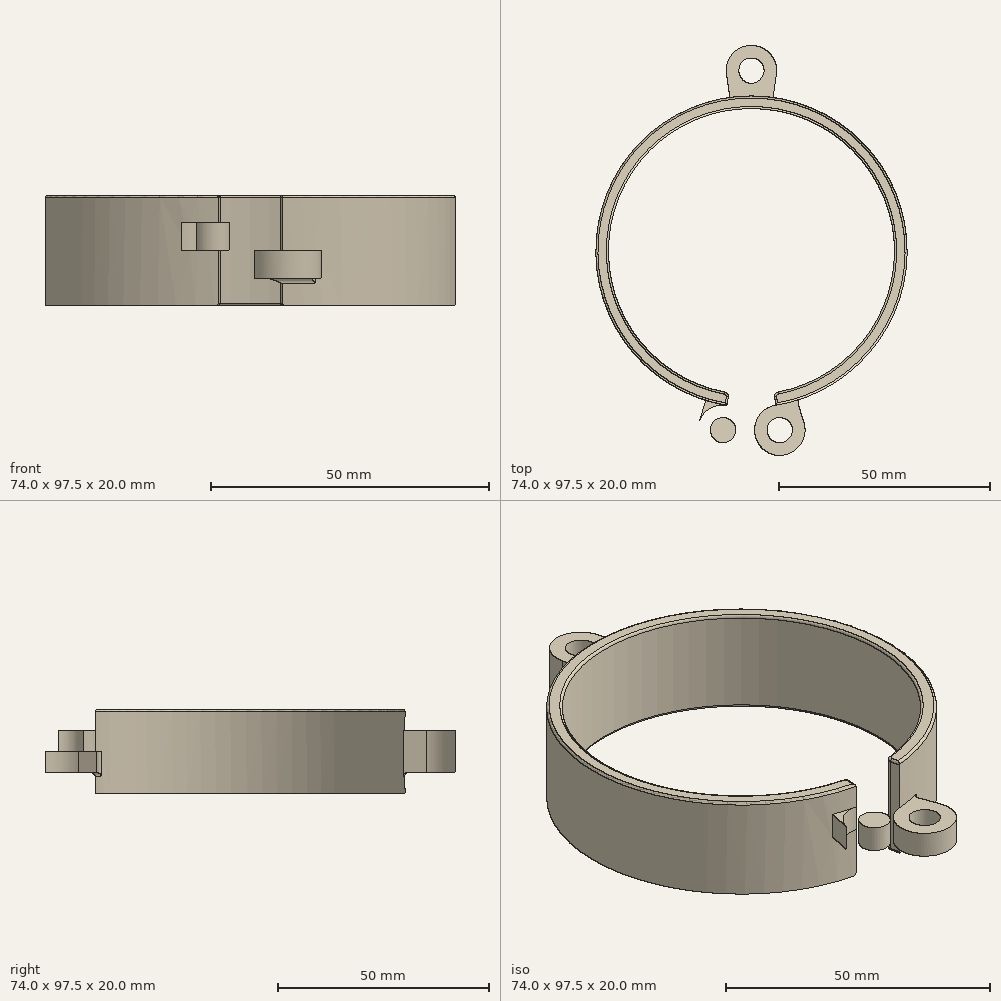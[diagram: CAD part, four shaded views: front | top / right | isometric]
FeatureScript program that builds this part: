
annotation { "Feature Type Name" : "Feature", "Feature Type Description" : "" }
export const myFeature = defineFeature(function(context is Context, id is Id, definition is map)
    precondition{}
    {
        {
            var Q0;
            Q0=qCreatedBy(makeId("Right.planeOp"),FACE);
            var sketch = newSketch(context, id + "F0", { "sketchPlane" : qUnion([Q0])});
            skLineSegment(sketch, "E0.bottom", {"start": v(34, 0) * mm, "end": v(37, 0) * mm});
            skLineSegment(sketch, "E0.top", {"start": v(34, 20) * mm, "end": v(37, 20) * mm});
            skLineSegment(sketch, "E0.left", {"start": v(34, 0) * mm, "end": v(34, 20) * mm});
            skLineSegment(sketch, "E0.right", {"start": v(37, 0) * mm, "end": v(37, 20) * mm});
            skLineSegment(sketch, "E1", {"start": v(0, 0) * mm, "end": v(0, 41.8) * mm, "construction": true});
            skSolve(sketch);
        }
        {
            var Q0;
            Q0=makeQuery(id+"F0.imprint","IMPRINT",FACE,{"disambiguationData":[TD([[makeQuery(id+"F0.imprint","IMPRINT",EDGE,{"derivedFrom":sQuery(id+"F0.wireOp",EDGE,"E0.bottom")}),1.0]])]});
            var Q1;
            Q1=sQuery(id+"F0.wireOp",EDGE,"E1");
            revolve(context, id + "F1", {"entities" : qUnion([Q0]), "axis" : qUnion([Q1]), "revolveType" : RevolveType.SYMMETRIC, "angle" : 342 * degree});
        }
        {
            var Q0;
            Q0=qCreatedBy(makeId("Top.planeOp"),FACE);
            var sketch = newSketch(context, id + "F2", { "sketchPlane" : qUnion([Q0])});
            skArc(sketch, "E2.0", {"start": v(-5.79, -36.54) * mm, "mid": v(0, 37) * mm, "end": v(5.79, -36.54) * mm});
            skLineSegment(sketch, "E3", {"start": v(0, 0) * mm, "end": v(0, -68.45) * mm, "construction": true});
            skLineSegment(sketch, "E4", {"start": v(0, 0) * mm, "end": v(0.74, -42.57) * mm, "construction": true});
            skLineSegment(sketch, "E5", {"start": v(10.84, -35.37) * mm, "end": v(12.48, -40.71) * mm});
            skCircle(sketch, "E6", {"center": v(6.74, -42.47) * mm, "radius": 6 * mm});
            skPoint(sketch, "E6.first.point", {"position": v(0.74, -42.57) * mm});
            skPoint(sketch, "E6.second.point", {"position": v(12.48, -40.71) * mm});
            skPoint(sketch, "E6.third.point", {"position": v(5.8, -36.54) * mm});
            skCircle(sketch, "E7.0", {"center": v(6.74, -42.47) * mm, "radius": 3 * mm});
            skLineSegment(sketch, "E8", {"start": v(5.79, -36.54) * mm, "end": v(5.79, -36.54) * mm});
            skCircle(sketch, "E9.MirrorC", {"center": v(-6.74, -42.47) * mm, "radius": 6 * mm});
            skCircle(sketch, "E10.MirrorC", {"center": v(-6.74, -42.47) * mm, "radius": 3 * mm});
            skLineSegment(sketch, "E11.MirrorCS", {"start": v(-10.84, -35.37) * mm, "end": v(-12.48, -40.71) * mm});
            skLineSegment(sketch, "E12.MirrorCS", {"start": v(-5.79, -36.54) * mm, "end": v(-5.79, -36.54) * mm});
            skPoint(sketch, "E13.orphan", {"position": v(20.87, -68.1) * mm});
            skPoint(sketch, "E14.orphan", {"position": v(-20.87, -68.1) * mm});
            skLineSegment(sketch, "E15", {"start": v(0, 0) * mm, "end": v(0, 59.86) * mm, "construction": true});
            skLineSegment(sketch, "E16", {"start": v(5.16, 36.64) * mm, "end": v(5.94, 42.16) * mm});
            skLineSegment(sketch, "E17.MirrorCS", {"start": v(-5.16, 36.64) * mm, "end": v(-5.94, 42.16) * mm});
            skCircle(sketch, "E18", {"center": v(0, 43) * mm, "radius": 6 * mm});
            skPoint(sketch, "E18.first.point", {"position": v(-5.94, 42.16) * mm});
            skPoint(sketch, "E18.second.point", {"position": v(5.94, 42.16) * mm});
            skPoint(sketch, "E18.third.point", {"position": v(0, 37) * mm});
            skCircle(sketch, "E19.0", {"center": v(0, 43) * mm, "radius": 3 * mm});
            skPoint(sketch, "E20.orphan", {"position": v(-8.52, 60.47) * mm});
            skPoint(sketch, "E21.orphan", {"position": v(8.52, 60.47) * mm});
            skLineSegment(sketch, "E22", {"start": v(0, 0) * mm, "end": v(6.74, -42.47) * mm, "construction": true});
            skSolve(sketch);
        }
        {
            var Q0;
            Q0=makeQuery(id+"F2.imprint","IMPRINT",FACE,{"disambiguationData":[TD([[makeQuery(id+"F2.imprint","IMPRINT",EDGE,{"derivedFrom":sQuery(id+"F2.wireOp",EDGE,"E7.0")}),-1.0]])]});
            var Q1;
            {var subQ0=sQuery(id+"F2.wireOp",EDGE,"E8");Q1=makeQuery(id+"F2.imprint","IMPRINT",FACE,{"disambiguationData":[TD([[makeQuery(id+"F2.imprint","IMPRINT",EDGE,{"derivedFrom":subQ0}),1.0]])]});}
            var Q2;
            {var subQ0=sQuery(id+"F2.wireOp",EDGE,"E5");Q2=makeQuery(id+"F2.imprint","IMPRINT",FACE,{"disambiguationData":[TD([[makeQuery(id+"F2.imprint","IMPRINT",EDGE,{"derivedFrom":subQ0}),-1.0]])]});}
            extrude(context, id + "F3", {"entities" : qUnion([Q0, Q1, Q2]), "operationType" : NewBodyOperationType.ADD, "depth" : 10 * mm});
        }
        {
            var Q0;
            {var subQ0=sQuery(id+"F2.wireOp",EDGE,"E12.MirrorCS");Q0=makeQuery(id+"F2.imprint","IMPRINT",FACE,{"disambiguationData":[TD([[makeQuery(id+"F2.imprint","IMPRINT",EDGE,{"derivedFrom":subQ0}),-1.0]])]});}
            var Q1;
            {var subQ0=sQuery(id+"F2.wireOp",EDGE,"E11.MirrorCS");Q1=makeQuery(id+"F2.imprint","IMPRINT",FACE,{"disambiguationData":[TD([[makeQuery(id+"F2.imprint","IMPRINT",EDGE,{"derivedFrom":subQ0}),1.0]])]});}
            var Q2;
            Q2=makeQuery(id+"F2.imprint","IMPRINT",FACE,{"disambiguationData":[TD([[makeQuery(id+"F2.imprint","IMPRINT",EDGE,{"derivedFrom":sQuery(id+"F2.wireOp",EDGE,"E10.MirrorC")}),1.0]])]});
            extrude(context, id + "F4", {"entities" : qUnion([Q0, Q1, Q2]), "operationType" : NewBodyOperationType.ADD, "depth" : 15 * mm});
        }
        {
            var Q0;
            {var subQ0=sQuery(id+"F2.wireOp",EDGE,"E12.MirrorCS");Q0=makeQuery(id+"F2.imprint","IMPRINT",FACE,{"disambiguationData":[TD([[makeQuery(id+"F2.imprint","IMPRINT",EDGE,{"derivedFrom":subQ0}),-1.0]])]});}
            var Q1;
            {var subQ0=sQuery(id+"F2.wireOp",EDGE,"E11.MirrorCS");Q1=makeQuery(id+"F2.imprint","IMPRINT",FACE,{"disambiguationData":[TD([[makeQuery(id+"F2.imprint","IMPRINT",EDGE,{"derivedFrom":subQ0}),1.0]])]});}
            var Q2;
            Q2=makeQuery(id+"F2.imprint","IMPRINT",FACE,{"disambiguationData":[TD([[makeQuery(id+"F2.imprint","IMPRINT",EDGE,{"derivedFrom":sQuery(id+"F2.wireOp",EDGE,"E10.MirrorC")}),1.0]])]});
            extrude(context, id + "F5", {"entities" : qUnion([Q0, Q1, Q2]), "operationType" : NewBodyOperationType.REMOVE, "depth" : 10 * mm});
        }
        {
            var Q0;
            {var subQ0=sQuery(id+"F2.wireOp",EDGE,"E8");Q0=makeQuery(id+"F2.imprint","IMPRINT",FACE,{"disambiguationData":[TD([[makeQuery(id+"F2.imprint","IMPRINT",EDGE,{"derivedFrom":subQ0}),1.0]])]});}
            var Q1;
            Q1=makeQuery(id+"F2.imprint","IMPRINT",FACE,{"disambiguationData":[TD([[makeQuery(id+"F2.imprint","IMPRINT",EDGE,{"derivedFrom":sQuery(id+"F2.wireOp",EDGE,"E7.0")}),-1.0]])]});
            var Q2;
            {var subQ0=sQuery(id+"F2.wireOp",EDGE,"E5");Q2=makeQuery(id+"F2.imprint","IMPRINT",FACE,{"disambiguationData":[TD([[makeQuery(id+"F2.imprint","IMPRINT",EDGE,{"derivedFrom":subQ0}),-1.0]])]});}
            extrude(context, id + "F6", {"entities" : qUnion([Q0, Q1, Q2]), "operationType" : NewBodyOperationType.REMOVE, "depth" : 5 * mm});
        }
        {
            var Q0;
            Q0=makeQuery(id+"F2.imprint","IMPRINT",FACE,{"disambiguationData":[TD([[makeQuery(id+"F2.imprint","IMPRINT",EDGE,{"derivedFrom":sQuery(id+"F2.wireOp",EDGE,"E19.0")}),-1.0]])]});
            var Q1;
            {var subQ0=sQuery(id+"F2.wireOp",EDGE,"E17.MirrorCS");Q1=makeQuery(id+"F2.imprint","IMPRINT",FACE,{"disambiguationData":[TD([[makeQuery(id+"F2.imprint","IMPRINT",EDGE,{"derivedFrom":subQ0}),-1.0]])]});}
            var Q2;
            {var subQ0=sQuery(id+"F2.wireOp",EDGE,"E16");Q2=makeQuery(id+"F2.imprint","IMPRINT",FACE,{"disambiguationData":[TD([[makeQuery(id+"F2.imprint","IMPRINT",EDGE,{"derivedFrom":subQ0}),1.0]])]});}
            extrude(context, id + "F7", {"entities" : qUnion([Q0, Q1, Q2]), "operationType" : NewBodyOperationType.ADD, "depth" : 15 * mm});
        }
        {
            var Q0;
            Q0=makeQuery(id+"F2.imprint","IMPRINT",FACE,{"disambiguationData":[TD([[makeQuery(id+"F2.imprint","IMPRINT",EDGE,{"derivedFrom":sQuery(id+"F2.wireOp",EDGE,"E19.0")}),1.0]])]});
            var Q1;
            Q1=makeQuery(id+"F2.imprint","IMPRINT",FACE,{"disambiguationData":[TD([[makeQuery(id+"F2.imprint","IMPRINT",EDGE,{"derivedFrom":sQuery(id+"F2.wireOp",EDGE,"E19.0")}),-1.0]])]});
            var Q2;
            {var subQ0=sQuery(id+"F2.wireOp",EDGE,"E17.MirrorCS");Q2=makeQuery(id+"F2.imprint","IMPRINT",FACE,{"disambiguationData":[TD([[makeQuery(id+"F2.imprint","IMPRINT",EDGE,{"derivedFrom":subQ0}),-1.0]])]});}
            var Q3;
            {var subQ0=sQuery(id+"F2.wireOp",EDGE,"E16");Q3=makeQuery(id+"F2.imprint","IMPRINT",FACE,{"disambiguationData":[TD([[makeQuery(id+"F2.imprint","IMPRINT",EDGE,{"derivedFrom":subQ0}),1.0]])]});}
            extrude(context, id + "F8", {"entities" : qUnion([Q0, Q1, Q2, Q3]), "operationType" : NewBodyOperationType.REMOVE, "depth" : 5 * mm});
        }
        {
            var Q0;
            Q0=makeQuery(id+"F1.opRevolve","CAP_EDGE",EDGE,{"disambiguationData":[OSD([sQuery(id+"F0.wireOp",EDGE,"E0.left")])],"isStart":true});
            var Q1;
            Q1=makeQuery(id+"F1.opRevolve","CAP_EDGE",EDGE,{"disambiguationData":[OSD([sQuery(id+"F0.wireOp",EDGE,"E0.left")])],"isStart":false});
            var Q2;
            Q2=makeQuery(id+"F3.opExtrude","SWEPT_EDGE",EDGE,{"disambiguationData":[OSD([sQuery(id+"F2.wireOp",EDGE,"E2.0"),sQuery(id+"F2.wireOp",EDGE,"E5")])]});
            var Q3;
            Q3=makeQuery(id+"F6.boolean.opBoolean","COPY",EDGE,{"derivedFrom":makeQuery(id+"F6.opExtrude","CAP_EDGE",EDGE,{"disambiguationData":[OSD([sQuery(id+"F2.wireOp",EDGE,"E2.0")])],"isStart":false})});
            var Q4;
            Q4=makeQuery(id+"F4.opExtrude","SWEPT_EDGE",EDGE,{"disambiguationData":[OSD([sQuery(id+"F2.wireOp",EDGE,"E2.0"),sQuery(id+"F2.wireOp",EDGE,"E11.MirrorCS")])]});
            var Q5;
            Q5=makeQuery(id+"F4.opExtrude","CAP_EDGE",EDGE,{"disambiguationData":[OSD([sQuery(id+"F2.wireOp",EDGE,"E2.0")])],"isStart":false});
            var Q6;
            Q6=makeQuery(id+"F7.opExtrude","SWEPT_EDGE",EDGE,{"disambiguationData":[OSD([sQuery(id+"F2.wireOp",EDGE,"E2.0"),sQuery(id+"F2.wireOp",EDGE,"E17.MirrorCS")])]});
            var Q7;
            Q7=makeQuery(id+"F7.opExtrude","SWEPT_EDGE",EDGE,{"disambiguationData":[OSD([sQuery(id+"F2.wireOp",EDGE,"E2.0"),sQuery(id+"F2.wireOp",EDGE,"E16")])]});
            var Q8;
            Q8=makeQuery(id+"F8.boolean.opBoolean","COPY",EDGE,{"derivedFrom":makeQuery(id+"F8.opExtrude","CAP_EDGE",EDGE,{"disambiguationData":[OSD([sQuery(id+"F2.wireOp",EDGE,"E2.0")])],"isStart":false})});
            var Q9;
            Q9=makeQuery(id+"F7.opExtrude","CAP_EDGE",EDGE,{"disambiguationData":[OSD([sQuery(id+"F2.wireOp",EDGE,"E2.0")])],"isStart":false});
            fillet(context, id + "F9", {"entities" : qUnion([Q0, Q1, Q2, Q3, Q4, Q5, Q6, Q7, Q8, Q9]), "radius" : 1 * mm, "tangentPropagation" : true, "allowEdgeOverflow" : false});
        }
        {
            var Q0;
            Q0=makeQuery(id+"F1.opRevolve","SWEPT_EDGE",EDGE,{"disambiguationData":[OSD([sQuery(id+"F0.wireOp",EDGE,"E0.top"),sQuery(id+"F0.wireOp",EDGE,"E0.left")])]});
            var Q1;
            Q1=makeQuery(id+"F1.opRevolve","SWEPT_EDGE",EDGE,{"disambiguationData":[OSD([sQuery(id+"F0.wireOp",EDGE,"E0.top"),sQuery(id+"F0.wireOp",EDGE,"E0.right")])]});
            var Q2;
            {var subQ0=sQuery(id+"F2.wireOp",EDGE,"E2.0");var subQ1=sQuery(id+"F2.wireOp",EDGE,"E6");var subQ2=sQuery(id+"F2.wireOp",EDGE,"E5");var subQ4=sQuery(id+"F0.wireOp",EDGE,"E0.right");var subQ7=sQuery(id+"F0.wireOp",EDGE,"E0.bottom");var subQ12=sQuery(id+"F2.wireOp",EDGE,"E9.MirrorC");var subQ16=sQuery(id+"F2.wireOp",EDGE,"E17.MirrorCS");var subQ17=sQuery(id+"F2.wireOp",EDGE,"E16");var subQ19=makeQuery(id+"F3.opExtrude","SWEPT_FACE",FACE,{"disambiguationData":[OSD([subQ2])]});var subQ20=makeQuery(id+"F1.opRevolve","SWEPT_EDGE",EDGE,{"disambiguationData":[OSD([subQ7,subQ4])]});var subQ21=makeQuery(id+"F3.boolean.opBoolean","SPLIT",EDGE,{"disambiguationData":[TD([subQ19])],"derivedFrom":subQ20});var subQ23=makeQuery(id+"F6.boolean.opBoolean","MERGE",EDGE,{"derivedFrom":[makeQuery(id+"F3.boolean.opBoolean","SPLIT",EDGE,{"disambiguationData":[TD([makeQuery(id+"F3.opExtrude","SWEPT_FACE",FACE,{"disambiguationData":[OSD([subQ1])]})])],"derivedFrom":subQ20}),makeQuery(id+"F5.boolean.opBoolean","MERGE",EDGE,{"derivedFrom":[makeQuery(id+"F4.boolean.opBoolean","SPLIT",EDGE,{"disambiguationData":[TD([makeQuery(id+"F4.opExtrude","SWEPT_FACE",FACE,{"disambiguationData":[OSD([subQ12])]})])],"derivedFrom":subQ21}),makeQuery(id+"F4.boolean.opBoolean","SPLIT",EDGE,{"disambiguationData":[TD([subQ19])],"derivedFrom":subQ21}),makeQuery(id+"F5.opExtrude","CAP_EDGE",EDGE,{"disambiguationData":[OSD([subQ0])],"isStart":true})]}),makeQuery(id+"F6.opExtrude","CAP_EDGE",EDGE,{"disambiguationData":[OSD([subQ0])],"isStart":true})]});Q2=makeQuery(id+"F8.boolean.opBoolean","MERGE",EDGE,{"derivedFrom":[makeQuery(id+"F7.boolean.opBoolean","SPLIT",EDGE,{"disambiguationData":[TD([makeQuery(id+"F7.opExtrude","SWEPT_FACE",FACE,{"disambiguationData":[OSD([subQ17])]})])],"derivedFrom":subQ23}),makeQuery(id+"F7.boolean.opBoolean","SPLIT",EDGE,{"disambiguationData":[TD([makeQuery(id+"F7.opExtrude","SWEPT_FACE",FACE,{"disambiguationData":[OSD([subQ16])]})])],"derivedFrom":subQ23}),makeQuery(id+"F8.opExtrude","CAP_EDGE",EDGE,{"disambiguationData":[OSD([subQ0])],"isStart":true})]});}
            var Q3;
            Q3=makeQuery(id+"F1.opRevolve","SWEPT_EDGE",EDGE,{"disambiguationData":[OSD([sQuery(id+"F0.wireOp",EDGE,"E0.bottom"),sQuery(id+"F0.wireOp",EDGE,"E0.left")])]});
            fillet(context, id + "F10", {"entities" : qUnion([Q0, Q1, Q2, Q3]), "radius" : .5 * mm, "tangentPropagation" : true, "allowEdgeOverflow" : false});
        }
    });
